# Revit family: QF_ELECTROLUXPROFESSIONAL_588116_MANABAHOOO
name_source: partatom
category: Specialty Equipment
units: mm (PartAtom-declared; Revit-internal decimal feet)

## family parameters
Always vertical = Yes
Cut with Voids When Loaded = No
Enable Cutting in Views = No
Maintain Annotation Orientation = No
Part Type = Normal
Room Calculation Point = No
Round Connector Dimension = Use Diameter
Shared = No
Work Plane-Based = No

## types (1)
- QF_ELECTROLUXPROFESSIONAL_588116_MANABAHOOO
    Accessory = No
    Default Elevation = 0 mm  [stored 0 ft]
    Depth Actual = 800 mm  [stored 2.62467 ft]
    Description = WORK TOP,CLOSED,1-SIDE,800X800X250H
    Direct Waste Size = 0"
    Gas KW = 0
    HP = 0 HP
    Height Actual = 250 mm  [stored 0.82021 ft]
    Length Actual = 800 mm  [stored 2.62467 ft]
    Manufacturer = Electrolux Professional
    Model = MANABAHOOO
    URL = http://www.electroluxprofessional.com
    URL Cutsheet = www.electrolux.com/professional
    URL Manufacturer = http://www.electroluxprofessional.com
    Watts = 0 W
    Weight = 20.00 kg
    Weight in Pounds = 44.09

note: [stored X ft] marks values corroborated as IEEE doubles in the binary element streams (Revit-internal decimal feet)

## geometry (parser evidence)
native form markers: Blend x9, Sweep x2
no freeform markers — native parametric forms only
